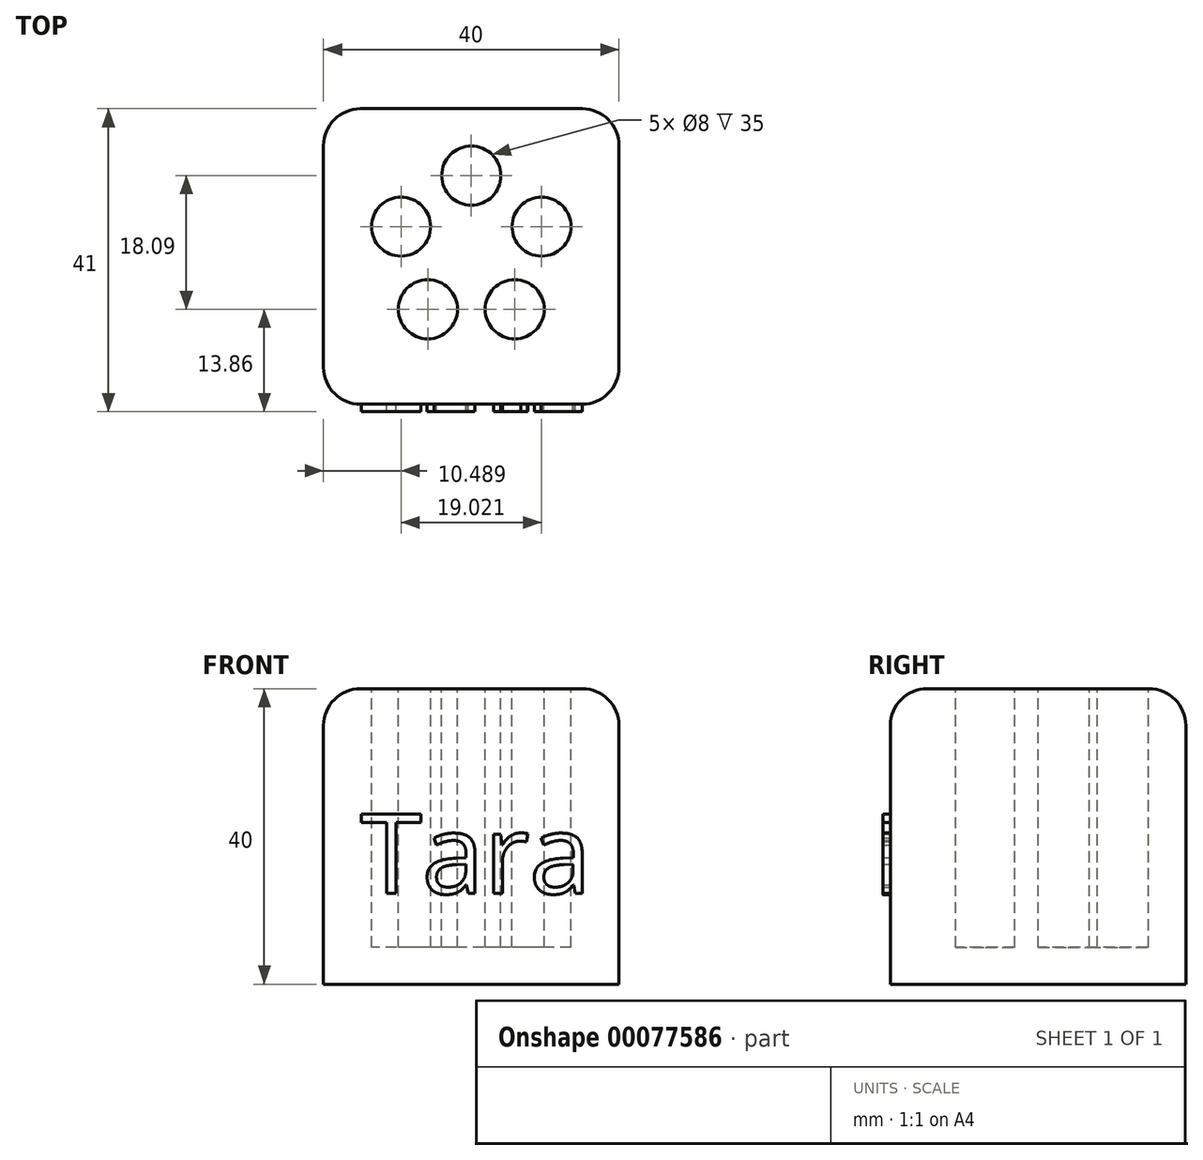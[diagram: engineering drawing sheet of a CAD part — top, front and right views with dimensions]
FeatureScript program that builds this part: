
annotation { "Feature Type Name" : "Feature", "Feature Type Description" : "" }
export const myFeature = defineFeature(function(context is Context, id is Id, definition is map)
    precondition{}
    {
        {
            var Q0;
            Q0=qCreatedBy(makeId("Right.planeOp"),FACE);
            var sketch = newSketch(context, id + "F0", { "sketchPlane" : qUnion([Q0])});
            skLineSegment(sketch, "E0", {"start": v(-20.95, 0) * mm, "end": v(19.05, 0) * mm});
            skLineSegment(sketch, "E1", {"start": v(19.05, 0) * mm, "end": v(19.05, 40) * mm});
            skLineSegment(sketch, "E2", {"start": v(19.05, 40) * mm, "end": v(-20.95, 40) * mm});
            skLineSegment(sketch, "E3", {"start": v(-20.95, 40) * mm, "end": v(-20.95, 0) * mm});
            skSolve(sketch);
        }
        {
            var Q0;
            Q0=makeQuery(id+"F0.imprint","IMPRINT",FACE,{"disambiguationData":[TD([[makeQuery(id+"F0.imprint","IMPRINT",EDGE,{"derivedFrom":sQuery(id+"F0.wireOp",EDGE,"E0")}),1.0]])]});
            extrude(context, id + "F1", {"entities" : qUnion([Q0]), "endBound" : BoundingType.SYMMETRIC, "depth" : 40 * mm});
        }
        {
            var Q0;
            Q0=makeQuery(id+"F1.opExtrude","SWEPT_FACE",FACE,{"disambiguationData":[OSD([sQuery(id+"F0.wireOp",EDGE,"E2")])]});
            var sketch = newSketch(context, id + "F2", { "sketchPlane" : qUnion([Q0])});
            skCircle(sketch, "E4", {"center": v(0, 0) * mm, "radius": 10 * mm, "construction": true});
            skCircle(sketch, "E5", {"center": v(0, 10) * mm, "radius": 4 * mm});
            skCircle(sketch, "E6.1.0", {"center": v(-9.51, 3.1) * mm, "radius": 4 * mm});
            skCircle(sketch, "E6.2.0", {"center": v(-5.88, -8.1) * mm, "radius": 4 * mm});
            skCircle(sketch, "E6.3.0", {"center": v(5.88, -8.1) * mm, "radius": 4 * mm});
            skCircle(sketch, "E6.4.0", {"center": v(9.51, 3.1) * mm, "radius": 4 * mm});
            skSolve(sketch);
        }
        {
            var Q0;
            Q0=makeQuery(id+"F1.opExtrude","CAP_EDGE",EDGE,{"disambiguationData":[OSD([sQuery(id+"F0.wireOp",EDGE,"E3")])],"isStart":false});
            var Q1;
            Q1=makeQuery(id+"F1.opExtrude","CAP_EDGE",EDGE,{"disambiguationData":[OSD([sQuery(id+"F0.wireOp",EDGE,"E1")])],"isStart":false});
            var Q2;
            Q2=makeQuery(id+"F1.opExtrude","CAP_EDGE",EDGE,{"disambiguationData":[OSD([sQuery(id+"F0.wireOp",EDGE,"E1")])],"isStart":true});
            var Q3;
            Q3=makeQuery(id+"F1.opExtrude","CAP_EDGE",EDGE,{"disambiguationData":[OSD([sQuery(id+"F0.wireOp",EDGE,"E3")])],"isStart":true});
            var Q4;
            Q4=makeQuery(id+"F1.opExtrude","SWEPT_EDGE",EDGE,{"disambiguationData":[OSD([sQuery(id+"F0.wireOp",EDGE,"E2"),sQuery(id+"F0.wireOp",EDGE,"E3")])]});
            var Q5;
            Q5=makeQuery(id+"F1.opExtrude","CAP_EDGE",EDGE,{"disambiguationData":[OSD([sQuery(id+"F0.wireOp",EDGE,"E2")])],"isStart":false});
            var Q6;
            Q6=makeQuery(id+"F1.opExtrude","SWEPT_EDGE",EDGE,{"disambiguationData":[OSD([sQuery(id+"F0.wireOp",EDGE,"E1"),sQuery(id+"F0.wireOp",EDGE,"E2")])]});
            var Q7;
            Q7=makeQuery(id+"F1.opExtrude","CAP_EDGE",EDGE,{"disambiguationData":[OSD([sQuery(id+"F0.wireOp",EDGE,"E2")])],"isStart":true});
            fillet(context, id + "F3", {"entities" : qUnion([Q0, Q1, Q2, Q3, Q4, Q5, Q6, Q7]), "radius" : 5 * mm, "tangentPropagation" : true, "allowEdgeOverflow" : false});
        }
        {
            var Q0;
            Q0 = qSketchRegion(id + "F2", true);
            extrude(context, id + "F4", {"entities" : qUnion([Q0]), "operationType" : NewBodyOperationType.REMOVE, "oppositeDirection" : true, "depth" : 35 * mm});
        }
        {
            var Q0;
            Q0=makeQuery(id+"F1.opExtrude","SWEPT_FACE",FACE,{"disambiguationData":[OSD([sQuery(id+"F0.wireOp",EDGE,"E3")])]});
            var sketch = newSketch(context, id + "F5", { "sketchPlane" : qUnion([Q0])});
            skText(sketch, "E7", { "text": "Tara", "fontName": "OpenSans-Regular.ttf"});
            const initialGuessF5  = {"E7": [-0.015, 0.01227, 1, 0, 0.01084]};
            skSetInitialGuess(sketch, initialGuessF5);
            skSolve(sketch);
        }
        {
            var Q0;
            Q0 = qSketchRegion(id + "F5", true);
            extrude(context, id + "F6", {"entities" : qUnion([Q0]), "operationType" : NewBodyOperationType.ADD, "depth" : 1 * mm});
        }
    });
